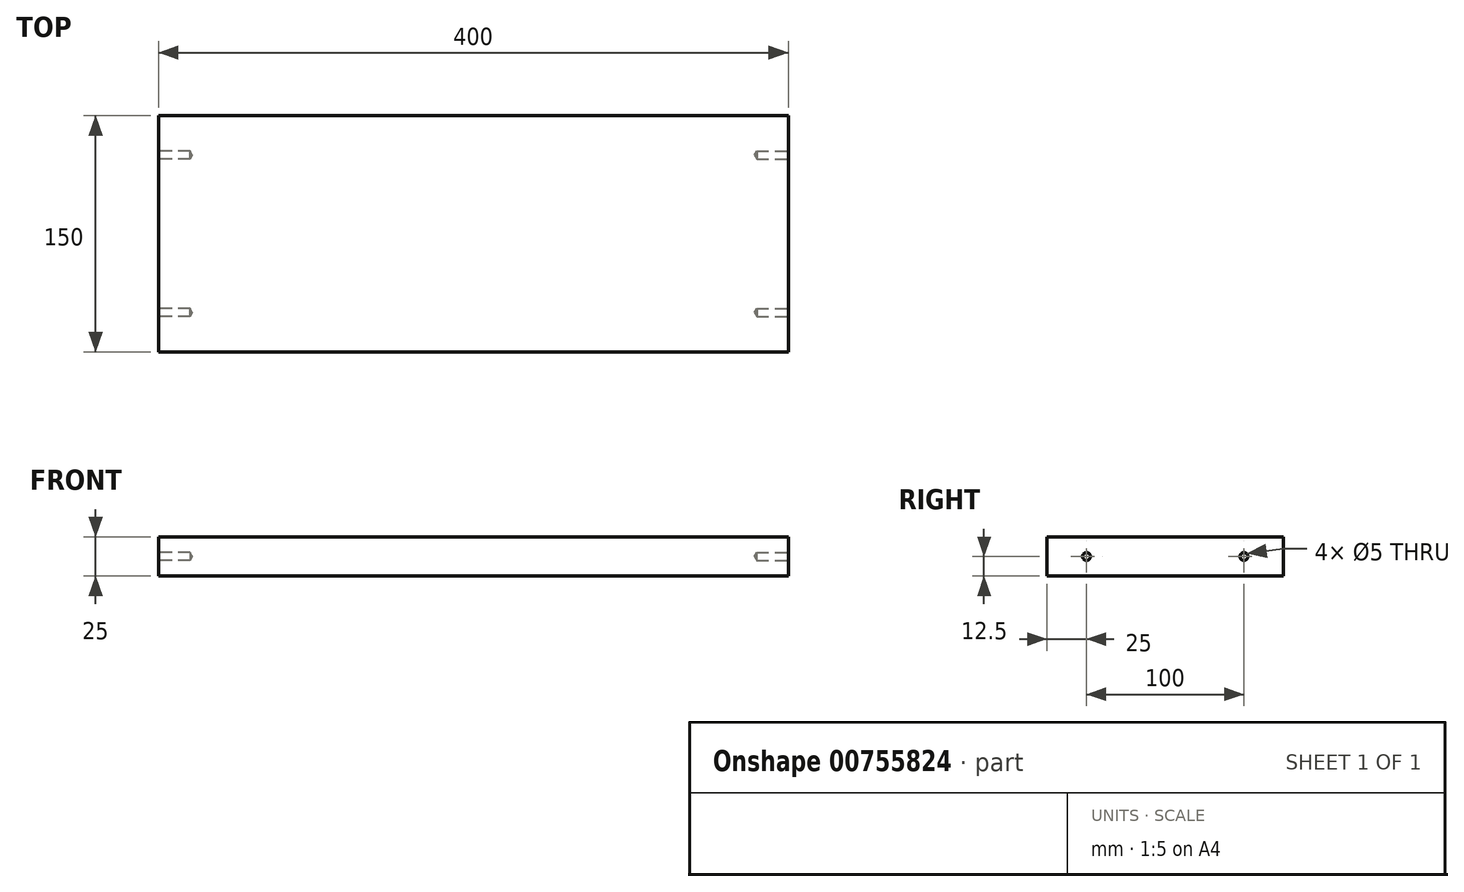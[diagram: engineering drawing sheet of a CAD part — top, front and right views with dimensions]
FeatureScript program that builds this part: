
annotation { "Feature Type Name" : "Feature", "Feature Type Description" : "" }
export const myFeature = defineFeature(function(context is Context, id is Id, definition is map)
    precondition{}
    {
        {
            var Q0;
            Q0=qCreatedBy(makeId("Top.planeOp"),FACE);
            var sketch = newSketch(context, id + "F0", { "sketchPlane" : qUnion([Q0])});
            skLineSegment(sketch, "E0.bottom", {"start": v(0, 0) * mm, "end": v(400, 0) * mm});
            skLineSegment(sketch, "E0.top", {"start": v(0, -150) * mm, "end": v(400, -150) * mm});
            skLineSegment(sketch, "E0.left", {"start": v(0, 0) * mm, "end": v(0, -150) * mm});
            skLineSegment(sketch, "E0.right", {"start": v(400, 0) * mm, "end": v(400, -150) * mm});
            skSolve(sketch);
        }
        {
            var Q0;
            Q0 = qSketchRegion(id + "F0", true);
            extrude(context, id + "F1", {"entities" : qUnion([Q0]), "depth" : 25 * mm, "offsetDistance" : 25 * mm});
        }
        {
            var Q0;
            Q0=makeQuery(id+"F1.opExtrude","SWEPT_FACE",FACE,{"disambiguationData":[OSD([sQuery(id+"F0.wireOp",EDGE,"E0.left")])]});
            var sketch = newSketch(context, id + "F2", { "sketchPlane" : qUnion([Q0])});
            skLineSegment(sketch, "E1", {"start": v(0, 12.5) * mm, "end": v(150, 12.5) * mm, "construction": true});
            skPoint(sketch, "E2.startSnap0", {"position": v(75, 12.5) * mm});
            skPoint(sketch, "E3", {"position": v(25, 12.5) * mm});
            skPoint(sketch, "E4", {"position": v(125, 12.5) * mm});
            skSolve(sketch);
        }
        {
            var Q0;
            Q0=sQuery(id+"F2.wireOp",VERTEX,"E3");
            var Q1;
            Q1=sQuery(id+"F2.wireOp",VERTEX,"E4");
            var Q2;
            Q2=makeQuery(id+"F1.opExtrude","SWEPT_BODY",BODY,{"disambiguationData":[OSD([sQuery(id+"F0.wireOp",EDGE,"E0.bottom"),sQuery(id+"F0.wireOp",EDGE,"E0.top"),sQuery(id+"F0.wireOp",EDGE,"E0.left"),sQuery(id+"F0.wireOp",EDGE,"E0.right")])]});
            hole(context, id + "F3", {"style" : HoleStyle.SIMPLE, "endStyle" : HoleEndStyle.BLIND, "holeDiameter" : 5 * mm, "majorDiameter" : 5 * mm, "holeDepth" : 20 * mm, "isTappedThrough" : true, "tappedDepth" : 12 * mm, "tapClearance" : 3, "locations" : qUnion([Q0, Q1]), "scope" : qUnion([Q2])});
        }
        {
            var Q0;
            Q0=makeQuery(id+"F1.opExtrude","SWEPT_FACE",FACE,{"disambiguationData":[OSD([sQuery(id+"F0.wireOp",EDGE,"E0.right")])]});
            var sketch = newSketch(context, id + "F4", { "sketchPlane" : qUnion([Q0])});
            skLineSegment(sketch, "E5", {"start": v(-150, 12.5) * mm, "end": v(0, 12.5) * mm, "construction": true});
            skPoint(sketch, "E6", {"position": v(-75, 12.5) * mm});
            skPoint(sketch, "E7", {"position": v(-125, 12.5) * mm});
            skPoint(sketch, "E8", {"position": v(-25, 12.5) * mm});
            skSolve(sketch);
        }
        {
            var Q0;
            Q0=sQuery(id+"F4.wireOp",VERTEX,"E7");
            var Q1;
            Q1=sQuery(id+"F4.wireOp",VERTEX,"E8");
            var Q2;
            Q2=makeQuery(id+"F1.opExtrude","SWEPT_BODY",BODY,{"disambiguationData":[OSD([sQuery(id+"F0.wireOp",EDGE,"E0.bottom"),sQuery(id+"F0.wireOp",EDGE,"E0.top"),sQuery(id+"F0.wireOp",EDGE,"E0.left"),sQuery(id+"F0.wireOp",EDGE,"E0.right")])]});
            hole(context, id + "F5", {"style" : HoleStyle.SIMPLE, "endStyle" : HoleEndStyle.BLIND, "holeDiameter" : 5 * mm, "majorDiameter" : 5 * mm, "holeDepth" : 20 * mm, "isTappedThrough" : true, "tappedDepth" : 12 * mm, "tapClearance" : 3, "locations" : qUnion([Q0, Q1]), "scope" : qUnion([Q2])});
        }
    });
